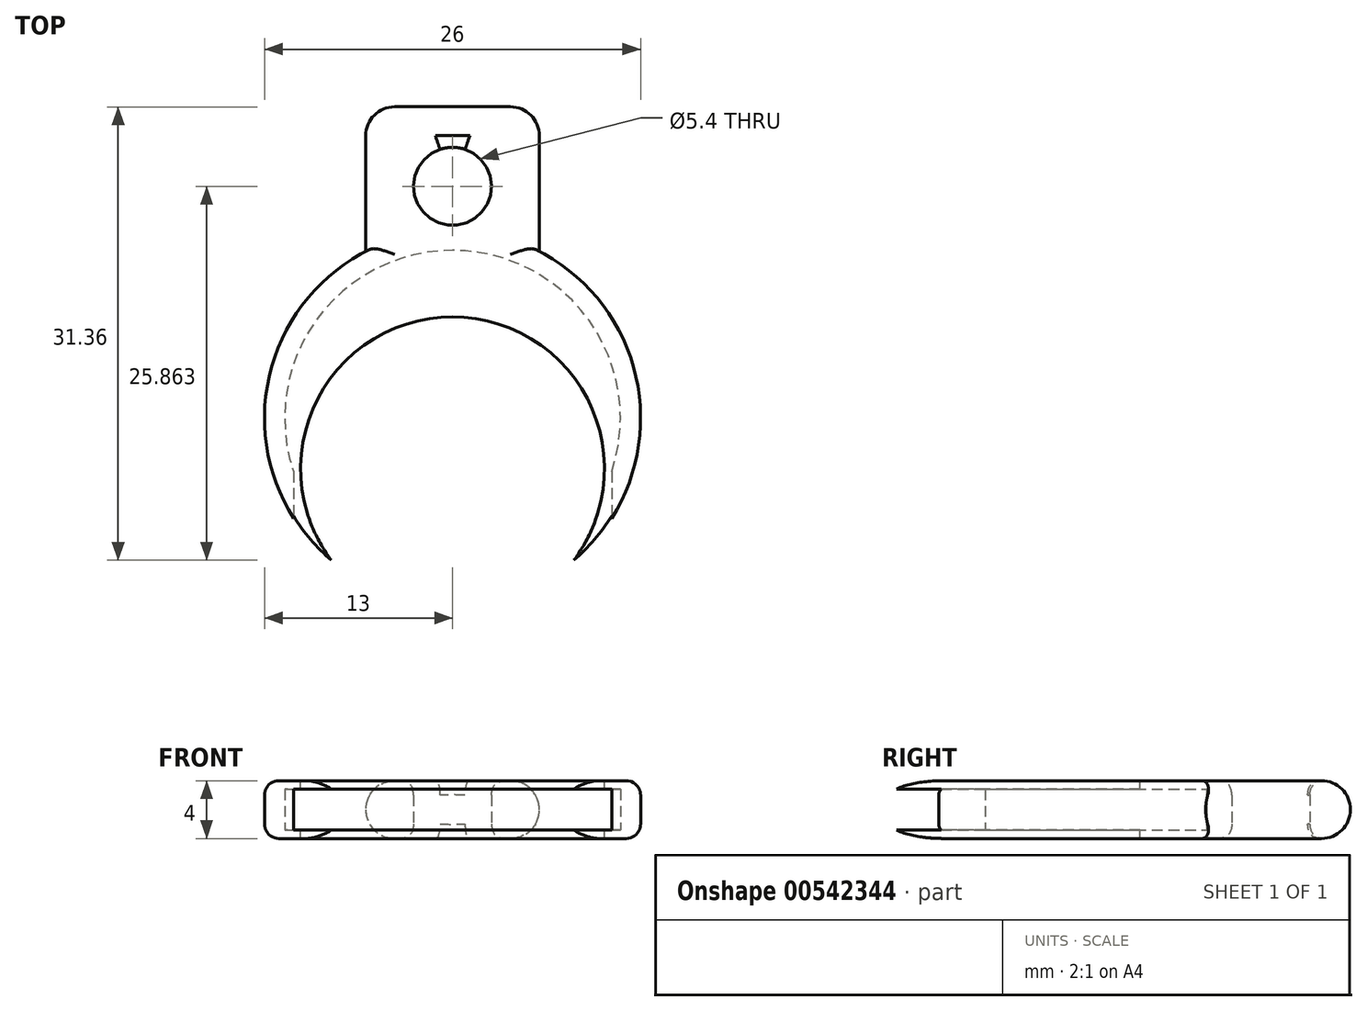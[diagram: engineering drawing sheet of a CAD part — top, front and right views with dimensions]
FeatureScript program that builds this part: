
annotation { "Feature Type Name" : "Feature", "Feature Type Description" : "" }
export const myFeature = defineFeature(function(context is Context, id is Id, definition is map)
    precondition{}
    {
        {
            var Q0;
            Q0=qCreatedBy(makeId("Top.planeOp"),FACE);
            var sketch = newSketch(context, id + "F0", { "sketchPlane" : qUnion([Q0])});
            skCircle(sketch, "E0", {"center": v(0, 0) * mm, "radius": 13 * mm});
            skLineSegment(sketch, "E1.bottom", {"start": v(-6, 11.53) * mm, "end": v(6, 11.53) * mm});
            skLineSegment(sketch, "E1.top", {"start": v(-6, 21.53) * mm, "end": v(6, 21.53) * mm});
            skLineSegment(sketch, "E1.left", {"start": v(-6, 11.53) * mm, "end": v(-6, 21.53) * mm});
            skLineSegment(sketch, "E1.right", {"start": v(6, 11.53) * mm, "end": v(6, 21.53) * mm});
            skCircle(sketch, "E2", {"center": v(0, 16.03) * mm, "radius": 2.7 * mm});
            skSolve(sketch);
        }
        {
            var Q0;
            Q0 = qSketchRegion(id + "F0", true);
            extrude(context, id + "F1", {"entities" : qUnion([Q0]), "endBound" : BoundingType.SYMMETRIC, "depth" : 4 * mm, "offsetDistance" : 25 * mm});
        }
        {
            var Q0;
            Q0=makeQuery(id+"F1.opExtrude","CAP_EDGE",EDGE,{"disambiguationData":[OSD([sQuery(id+"F0.wireOp",EDGE,"E1.right")])],"isStart":true});
            var Q1;
            Q1=makeQuery(id+"F1.opExtrude","CAP_EDGE",EDGE,{"disambiguationData":[OSD([sQuery(id+"F0.wireOp",EDGE,"E1.left")])],"isStart":true});
            var Q2;
            Q2=makeQuery(id+"F1.opExtrude","CAP_EDGE",EDGE,{"disambiguationData":[OSD([sQuery(id+"F0.wireOp",EDGE,"E1.left")])],"isStart":false});
            var Q3;
            Q3=makeQuery(id+"F1.opExtrude","CAP_EDGE",EDGE,{"disambiguationData":[OSD([sQuery(id+"F0.wireOp",EDGE,"E1.right")])],"isStart":false});
            var Q4;
            Q4=makeQuery(id+"F1.opExtrude","CAP_EDGE",EDGE,{"disambiguationData":[OSD([sQuery(id+"F0.wireOp",EDGE,"E1.top")])],"isStart":true});
            var Q5;
            Q5=makeQuery(id+"F1.opExtrude","CAP_EDGE",EDGE,{"disambiguationData":[OSD([sQuery(id+"F0.wireOp",EDGE,"E1.top")])],"isStart":false});
            var Q6;
            Q6=makeQuery(id+"F1.opExtrude","SWEPT_EDGE",EDGE,{"disambiguationData":[OSD([sQuery(id+"F0.wireOp",EDGE,"E1.top"),sQuery(id+"F0.wireOp",EDGE,"E1.left")])]});
            var Q7;
            Q7=makeQuery(id+"F1.opExtrude","SWEPT_EDGE",EDGE,{"disambiguationData":[OSD([sQuery(id+"F0.wireOp",EDGE,"E1.top"),sQuery(id+"F0.wireOp",EDGE,"E1.right")])]});
            fillet(context, id + "F2", {"entities" : qUnion([Q0, Q1, Q2, Q3, Q4, Q5, Q6, Q7]), "radius" : 2 * mm, "tangentPropagation" : true, "allowEdgeOverflow" : false});
        }
        {
            var Q0;
            Q0=makeQuery(id+"F1.opExtrude","CAP_FACE",FACE,{"disambiguationData":[OSD([sQuery(id+"F0.wireOp",EDGE,"E0"),sQuery(id+"F0.wireOp",EDGE,"E1.top"),sQuery(id+"F0.wireOp",EDGE,"E1.left"),sQuery(id+"F0.wireOp",EDGE,"E1.right"),sQuery(id+"F0.wireOp",EDGE,"E2")])],"isStart":false});
            var sketch = newSketch(context, id + "F3", { "sketchPlane" : qUnion([Q0])});
            skCircle(sketch, "E3", {"center": v(0, -3.5) * mm, "radius": 10.5 * mm});
            skSolve(sketch);
        }
        {
            var Q0;
            {var subQ0=sQuery(id+"F3.wireOp",EDGE,"E3");var subQ1=makeQuery(id+"F1.opExtrude","CAP_EDGE",EDGE,{"disambiguationData":[OSD([sQuery(id+"F0.wireOp",EDGE,"E0")])],"isStart":false});var subQ2=makeQuery(id+"F3.imprint","INTERSECT",VERTEX,{"disambiguationData":[OD(0.0)],"derivedFrom":[subQ1,subQ0]});Q0=makeQuery(id+"F3.imprint","IMPRINT",FACE,{"disambiguationData":[TD([[makeQuery(id+"F3.imprint","IMPRINT",EDGE,{"disambiguationData":[TD([[subQ2,1.0]])],"derivedFrom":subQ0}),1.0]])]});}
            extrude(context, id + "F4", {"entities" : qUnion([Q0]), "operationType" : NewBodyOperationType.REMOVE, "endBound" : BoundingType.THROUGH_ALL, "oppositeDirection" : true, "depth" : 30 * mm, "offsetDistance" : 25 * mm});
        }
        {
            var Q0;
            Q0=qCreatedBy(makeId("Top.planeOp"),FACE);
            var sketch = newSketch(context, id + "F5", { "sketchPlane" : qUnion([Q0])});
            skCircle(sketch, "E4", {"center": v(0, 0) * mm, "radius": 11.6 * mm});
            skLineSegment(sketch, "E5.bottom", {"start": v(-11, -3.7) * mm, "end": v(11, -3.7) * mm});
            skLineSegment(sketch, "E5.top", {"start": v(-11, -16.9) * mm, "end": v(11, -16.9) * mm});
            skLineSegment(sketch, "E5.left", {"start": v(-11, -3.7) * mm, "end": v(-11, -16.9) * mm});
            skLineSegment(sketch, "E5.right", {"start": v(11, -3.7) * mm, "end": v(11, -16.9) * mm});
            skSolve(sketch);
        }
        {
            var Q0;
            Q0=makeQuery(id+"F5.imprint","IMPRINT",FACE,{"disambiguationData":[TD([[makeQuery(id+"F5.imprint","IMPRINT",EDGE,{"derivedFrom":sQuery(id+"F5.wireOp",EDGE,"E4")}),1.0]])]});
            var Q1;
            Q1=sQuery(id+"F5.wireOp",EDGE,"E4");
            extrude(context, id + "F6", {"entities" : qUnion([Q0]), "operationType" : NewBodyOperationType.REMOVE, "surfaceEntities" : qUnion([Q1]), "endBound" : BoundingType.SYMMETRIC, "depth" : 2.8 * mm, "offsetDistance" : 25 * mm});
        }
        {
            var Q0;
            Q0=makeQuery(id+"F1.opExtrude","CAP_EDGE",EDGE,{"disambiguationData":[OSD([sQuery(id+"F0.wireOp",EDGE,"E2")])],"isStart":false});
            var Q1;
            Q1=makeQuery(id+"F1.opExtrude","CAP_EDGE",EDGE,{"disambiguationData":[OSD([sQuery(id+"F0.wireOp",EDGE,"E2")])],"isStart":true});
            fillet(context, id + "F7", {"entities" : qUnion([Q0, Q1]), "radius" : 1 * mm, "rho" : 0.5, "crossSection" : FilletCrossSection.CONIC, "allowEdgeOverflow" : false});
        }
        {
            var Q0;
            Q0 = qSketchRegion(id + "F5", true);
            extrude(context, id + "F8", {"entities" : qUnion([Q0]), "operationType" : NewBodyOperationType.REMOVE, "endBound" : BoundingType.SYMMETRIC, "depth" : 2.8 * mm, "offsetDistance" : 25 * mm});
        }
        {
            var Q0;
            {var subQ0=sQuery(id+"F0.wireOp",EDGE,"E0");var subQ1=sQuery(id+"F0.wireOp",EDGE,"E1.left");Q0=makeQuery(id+"F4.boolean.opBoolean","SPLIT",EDGE,{"disambiguationData":[TD([makeQuery(id+"F2.opFillet","BLEND_FACE",FACE,{"disambiguationData":[OSD([subQ1])]})])],"derivedFrom":makeQuery(id+"F1.opExtrude","CAP_EDGE",EDGE,{"disambiguationData":[OSD([subQ0])],"isStart":false})});}
            var Q1;
            {var subQ0=sQuery(id+"F0.wireOp",EDGE,"E0");var subQ1=sQuery(id+"F0.wireOp",EDGE,"E1.right");Q1=makeQuery(id+"F4.boolean.opBoolean","SPLIT",EDGE,{"disambiguationData":[TD([makeQuery(id+"F2.opFillet","BLEND_FACE",FACE,{"disambiguationData":[OSD([subQ1])]})])],"derivedFrom":makeQuery(id+"F1.opExtrude","CAP_EDGE",EDGE,{"disambiguationData":[OSD([subQ0])],"isStart":false})});}
            var Q2;
            {var subQ0=sQuery(id+"F0.wireOp",EDGE,"E0");var subQ1=sQuery(id+"F0.wireOp",EDGE,"E1.left");Q2=makeQuery(id+"F4.boolean.opBoolean","SPLIT",EDGE,{"disambiguationData":[TD([makeQuery(id+"F2.opFillet","BLEND_FACE",FACE,{"disambiguationData":[OSD([subQ1])]})])],"derivedFrom":makeQuery(id+"F1.opExtrude","CAP_EDGE",EDGE,{"disambiguationData":[OSD([subQ0])],"isStart":true})});}
            var Q3;
            {var subQ0=sQuery(id+"F0.wireOp",EDGE,"E0");var subQ1=sQuery(id+"F0.wireOp",EDGE,"E1.right");Q3=makeQuery(id+"F4.boolean.opBoolean","SPLIT",EDGE,{"disambiguationData":[TD([makeQuery(id+"F2.opFillet","BLEND_FACE",FACE,{"disambiguationData":[OSD([subQ1])]})])],"derivedFrom":makeQuery(id+"F1.opExtrude","CAP_EDGE",EDGE,{"disambiguationData":[OSD([subQ0])],"isStart":true})});}
            fillet(context, id + "F9", {"entities" : qUnion([Q0, Q1, Q2, Q3]), "radius" : 1 * mm, "tangentPropagation" : true, "allowEdgeOverflow" : false});
        }
    });
